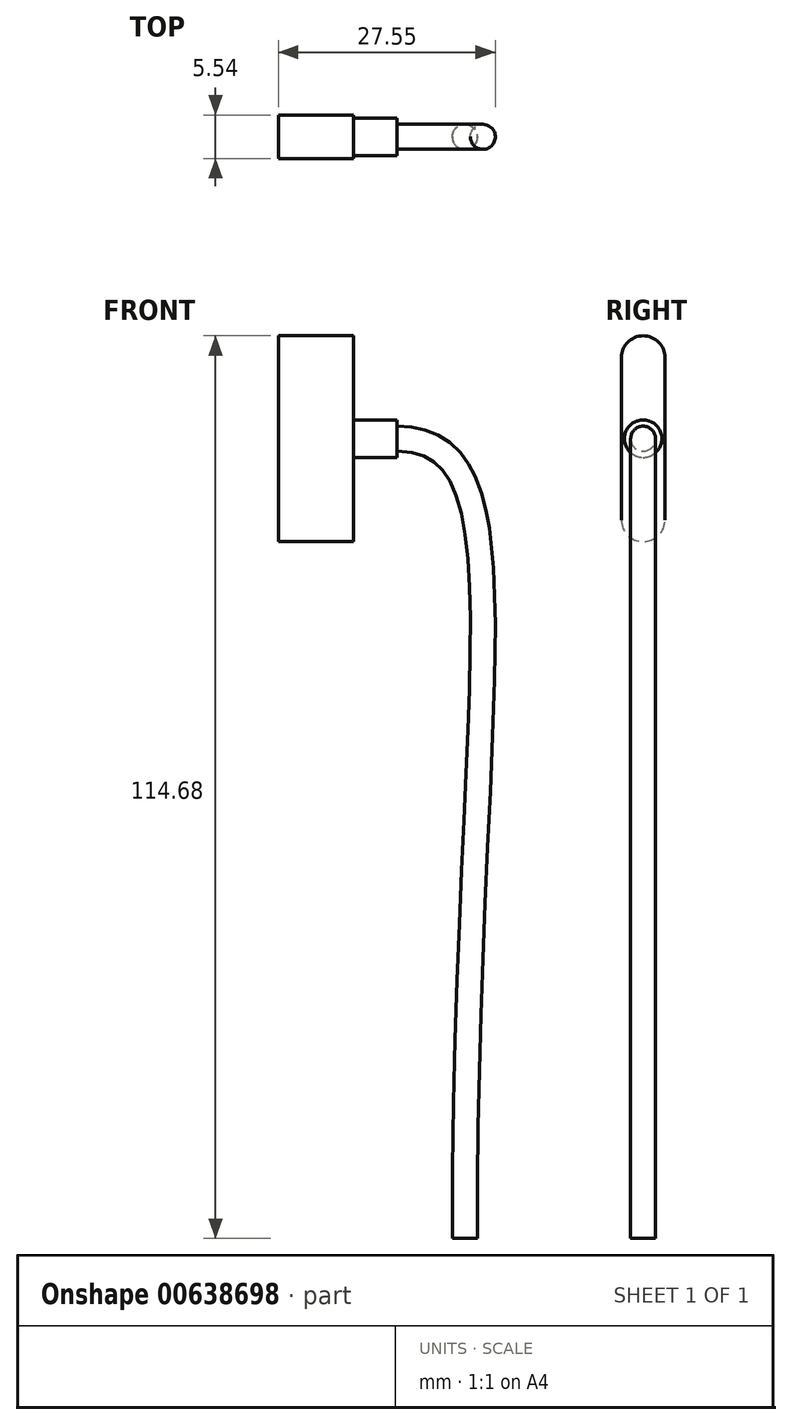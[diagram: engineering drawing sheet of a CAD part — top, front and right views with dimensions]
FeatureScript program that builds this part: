
annotation { "Feature Type Name" : "Feature", "Feature Type Description" : "" }
export const myFeature = defineFeature(function(context is Context, id is Id, definition is map)
    precondition{}
    {
        {
            var Q0;
            Q0=qCreatedBy(makeId("Right.planeOp"),FACE);
            var sketch = newSketch(context, id + "F0", { "sketchPlane" : qUnion([Q0])});
            skLineSegment(sketch, "E0.left", {"start": v(2.77, 10.31) * mm, "end": v(2.77, -10.31) * mm});
            skLineSegment(sketch, "E0.right", {"start": v(-2.77, 10.31) * mm, "end": v(-2.77, -10.31) * mm});
            skPoint(sketch, "E0.middle", {"position": v(0, 0) * mm});
            skPoint(sketch, "E1", {"position": v(-2.77, 10.31) * mm});
            skLineSegment(sketch, "E2", {"start": v(-2.77, 10.31) * mm, "end": v(2.77, 10.31) * mm, "construction": true});
            skPoint(sketch, "E3", {"position": v(0, 13.08) * mm});
            skArc(sketch, "E4", {"start": v(2.77, 10.31) * mm, "mid": v(0, 13.08) * mm, "end": v(-2.77, 10.31) * mm});
            skPoint(sketch, "E5.orphan", {"position": v(-2.77, 13.08) * mm});
            skPoint(sketch, "E6.orphan", {"position": v(2.77, 13.08) * mm});
            skPoint(sketch, "E7", {"position": v(-2.77, -10.31) * mm});
            skLineSegment(sketch, "E8", {"start": v(-2.77, -10.31) * mm, "end": v(2.77, -10.31) * mm, "construction": true});
            skPoint(sketch, "E9", {"position": v(0, -13.08) * mm});
            skArc(sketch, "E10", {"start": v(-2.77, -10.31) * mm, "mid": v(0, -13.08) * mm, "end": v(2.77, -10.31) * mm});
            skPoint(sketch, "E11.orphan", {"position": v(-2.77, -13.08) * mm});
            skPoint(sketch, "E12.orphan", {"position": v(2.77, -13.08) * mm});
            skSolve(sketch);
        }
        {
            var Q0;
            Q0 = qSketchRegion(id + "F0", true);
            extrude(context, id + "F1", {"entities" : qUnion([Q0]), "depth" : 9.52 * mm, "offsetDistance" : 25.4 * mm});
        }
        {
            var Q0;
            Q0=makeQuery(id+"F1.opExtrude","CAP_FACE",FACE,{"disambiguationData":[OSD([sQuery(id+"F0.wireOp",EDGE,"E0.left"),sQuery(id+"F0.wireOp",EDGE,"E0.right"),sQuery(id+"F0.wireOp",EDGE,"E4"),sQuery(id+"F0.wireOp",EDGE,"E10")])],"isStart":false});
            var sketch = newSketch(context, id + "F2", { "sketchPlane" : qUnion([Q0])});
            skCircle(sketch, "E13", {"center": v(0, 0) * mm, "radius": 2.38 * mm});
            skSolve(sketch);
        }
        {
            var Q0;
            Q0 = qSketchRegion(id + "F2", true);
            extrude(context, id + "F3", {"entities" : qUnion([Q0]), "operationType" : NewBodyOperationType.ADD, "depth" : 5.56 * mm, "offsetDistance" : 25.4 * mm});
        }
        {
            var Q0;
            Q0=makeQuery(id+"F3.opExtrude","CAP_FACE",FACE,{"disambiguationData":[OSD([sQuery(id+"F2.wireOp",EDGE,"E13")])],"isStart":false});
            var sketch = newSketch(context, id + "F4", { "sketchPlane" : qUnion([Q0])});
            skCircle(sketch, "E14", {"center": v(0, 0) * mm, "radius": 1.59 * mm});
            skSolve(sketch);
        }
        {
            var Q0;
            Q0=qCreatedBy(makeId("Top.planeOp"),FACE);
            cPlane(context, id + "F5", {"entities" : qUnion([Q0]), "cplaneType" : CPlaneType.OFFSET, "offset" : 101.6 * mm, "oppositeDirection" : true, "width" : 152.4 * mm, "height" : 152.4 * mm});
        }
        {
            var Q0;
            Q0=qCreatedBy(id+"F5.planeOp",FACE);
            var sketch = newSketch(context, id + "F6", { "sketchPlane" : qUnion([Q0])});
            skLineSegment(sketch, "E15.0", {"start": v(15.08, 1.59) * mm, "end": v(15.08, -1.59) * mm, "construction": true});
            skPoint(sketch, "E16.0", {"position": v(15.08, 0) * mm});
            skLineSegment(sketch, "E17", {"start": v(15.08, 0) * mm, "end": v(23.66, 0) * mm, "construction": true});
            skCircle(sketch, "E18", {"center": v(23.66, 0) * mm, "radius": 1.59 * mm});
            skSolve(sketch);
        }
        {
            var Q0;
            Q0=qCreatedBy(makeId("Front.planeOp"),FACE);
            var sketch = newSketch(context, id + "F7", { "sketchPlane" : qUnion([Q0])});
            skPoint(sketch, "E19.0", {"position": v(15.08, 0) * mm});
            skPoint(sketch, "E20.0", {"position": v(23.66, -101.6) * mm});
            skFitSpline(sketch, "E21", {"points": [v(23.66, -101.6) * mm, v(15.08, 0) * mm], "startDerivative": vector(-0.23, 207.23) * mm, "endDerivative": vector(-52.92, 0) * mm});
            skSolve(sketch);
        }
        {
            var Q0;
            Q0=makeQuery(id+"F4.imprint","IMPRINT",FACE,{"disambiguationData":[TD([[makeQuery(id+"F4.imprint","IMPRINT",EDGE,{"derivedFrom":sQuery(id+"F4.wireOp",EDGE,"E14")}),1.0]])]});
            var Q1;
            Q1=sQuery(id+"F7.wireOp",EDGE,"E21");
            sweep(context, id + "F8", {"operationType" : NewBodyOperationType.ADD, "profiles" : qUnion([Q0]), "path" : qUnion([Q1])});
        }
    });
